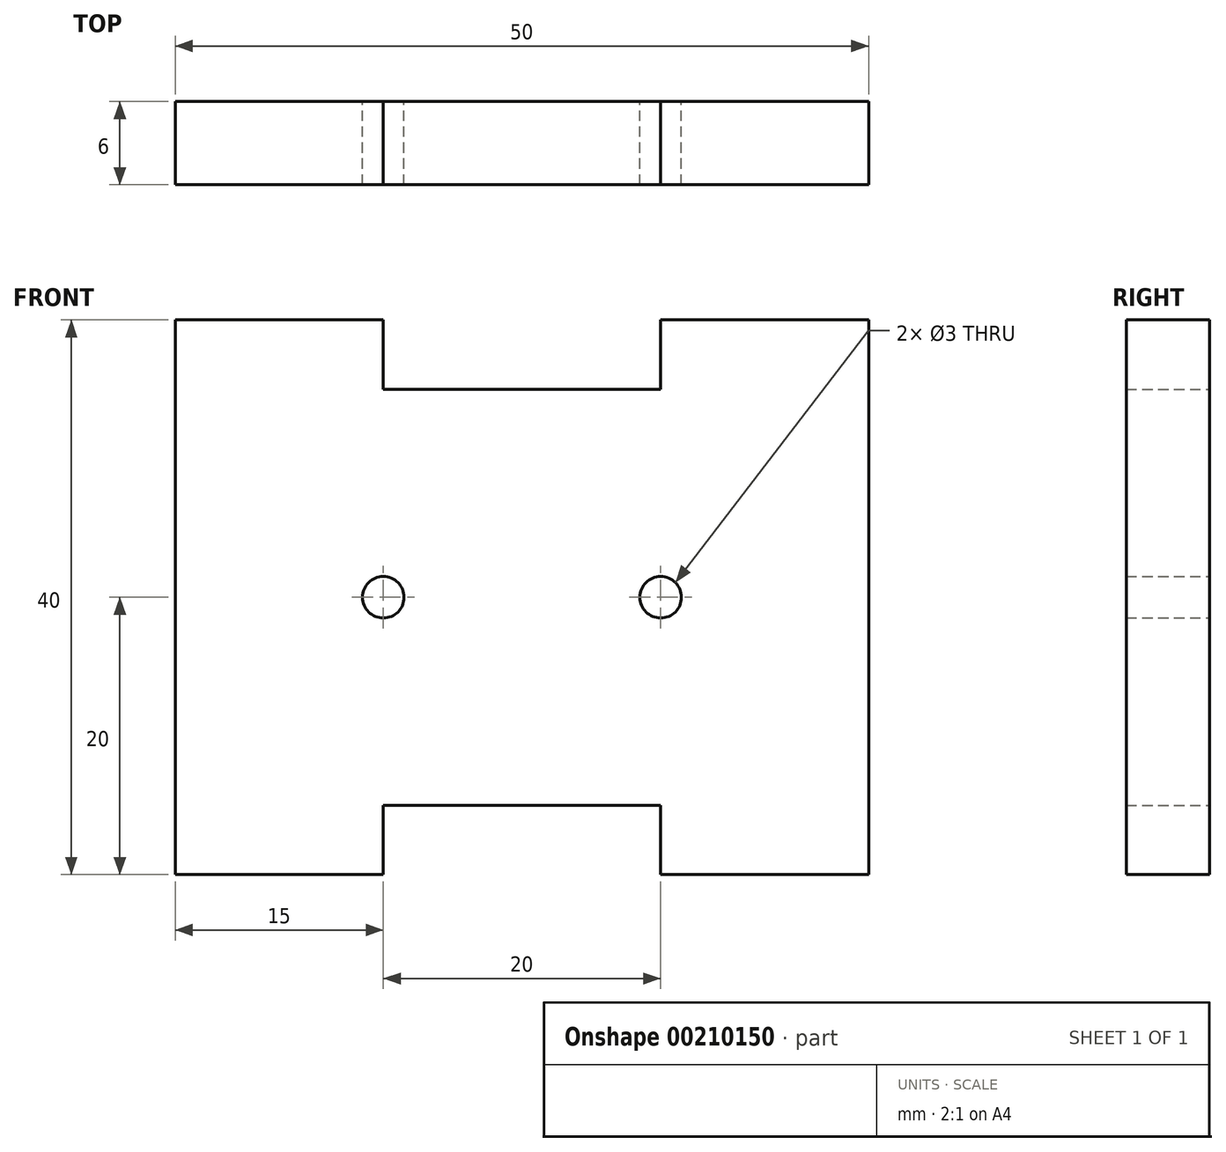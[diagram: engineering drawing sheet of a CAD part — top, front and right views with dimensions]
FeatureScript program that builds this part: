
annotation { "Feature Type Name" : "Feature", "Feature Type Description" : "" }
export const myFeature = defineFeature(function(context is Context, id is Id, definition is map)
    precondition{}
    {
        {
            var Q0;
            Q0=qCreatedBy(makeId("Front.planeOp"),FACE);
            var sketch = newSketch(context, id + "F0", { "sketchPlane" : qUnion([Q0])});
            skLineSegment(sketch, "E0.bottom", {"start": v(15, 0) * mm, "end": v(35, 0) * mm});
            skLineSegment(sketch, "E0.top", {"start": v(15, 30) * mm, "end": v(35, 30) * mm});
            skLineSegment(sketch, "E0.left", {"start": v(0, 0) * mm, "end": v(0, 30) * mm});
            skLineSegment(sketch, "E0.right", {"start": v(50, 0) * mm, "end": v(50, 30) * mm});
            skCircle(sketch, "E1", {"center": v(15, 15) * mm, "radius": 1.5 * mm});
            skCircle(sketch, "E2", {"center": v(35, 15) * mm, "radius": 1.5 * mm});
            skLineSegment(sketch, "E3.top", {"start": v(0, 35) * mm, "end": v(15, 35) * mm});
            skLineSegment(sketch, "E3.left", {"start": v(0, 30) * mm, "end": v(0, 35) * mm});
            skLineSegment(sketch, "E3.right", {"start": v(15, 30) * mm, "end": v(15, 35) * mm});
            skLineSegment(sketch, "E4.top", {"start": v(35, 35) * mm, "end": v(50, 35) * mm});
            skLineSegment(sketch, "E4.left", {"start": v(35, 30) * mm, "end": v(35, 35) * mm});
            skLineSegment(sketch, "E4.right", {"start": v(50, 30) * mm, "end": v(50, 35) * mm});
            skLineSegment(sketch, "E5", {"start": v(0, 15) * mm, "end": v(50, 15) * mm, "construction": true});
            skLineSegment(sketch, "E6.MirrorCS", {"start": v(35, -5) * mm, "end": v(50, -5) * mm});
            skLineSegment(sketch, "E7.MirrorCS", {"start": v(15, 0) * mm, "end": v(15, -5) * mm});
            skLineSegment(sketch, "E8.MirrorCS", {"start": v(0, 0) * mm, "end": v(0, -5) * mm});
            skLineSegment(sketch, "E9.MirrorCS", {"start": v(0, -5) * mm, "end": v(15, -5) * mm});
            skLineSegment(sketch, "E10.MirrorCS", {"start": v(35, 0) * mm, "end": v(35, -5) * mm});
            skLineSegment(sketch, "E11.MirrorCS", {"start": v(50, 0) * mm, "end": v(50, -5) * mm});
            skPoint(sketch, "E12.orphan", {"position": v(50, 0) * mm});
            skLineSegment(sketch, "E13", {"start": v(0, 0) * mm, "end": v(50, 0) * mm, "construction": true});
            skLineSegment(sketch, "E14", {"start": v(0, 30) * mm, "end": v(50, 30) * mm, "construction": true});
            skSolve(sketch);
        }
        {
            var Q0;
            Q0=makeQuery(id+"F0.imprint","IMPRINT",FACE,{"disambiguationData":[TD([[makeQuery(id+"F0.imprint","IMPRINT",EDGE,{"derivedFrom":sQuery(id+"F0.wireOp",EDGE,"E0.top")}),-1.0]])]});
            extrude(context, id + "F1", {"entities" : qUnion([Q0]), "depth" : 6 * mm});
        }
    });
